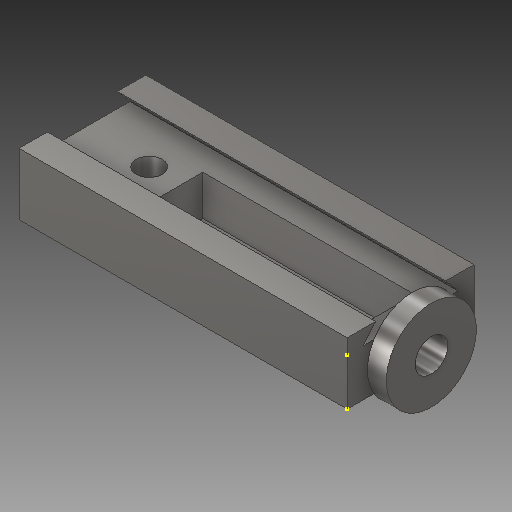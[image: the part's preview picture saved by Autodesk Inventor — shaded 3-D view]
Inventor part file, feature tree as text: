
AUTODESK INVENTOR PART (.ipt)
format: ipt  version: 2018 (Build 220112000, 112)  size: 252,928 bytes
history: native  units: mm
features: sketch x12, extrude x10
ambient origin geometry x8: Origin, YZ Plane, XZ Plane, XY Plane, X Axis, Y Axis, Z Axis, Center Point
bodies: Solid1 (feature_tree)
feature tree (22):
  extrude  "Extrusion1"  Depth=41.4mm
  extrude  "Extrusion2"  Depth=220.0mm
  extrude  "Extrusion3"  Depth=301.25mm TaperAngle=0.0deg
  sketch  "Sketch4"  dims[d12=15.1mm d13=15.1mm]
  extrude  "Extrusion4"  Depth=15.1mm
  sketch  "Sketch6"  dims[d17=28.6mm d18=30.2mm]
  extrude  "Extrusion5"  Depth=26.9mm TaperAngle=0.0deg
  extrude  "Extrusion6"  Depth=30.2mm
  extrude  "Extrusion7"  Depth=11.0mm
  extrude  "Extrusion8"  Depth=60.4mm
  extrude  "Extrusion9"  Depth=12.7mm
  extrude  "Extrusion10"  TaperAngle=90.0deg  [1 undecoded]
  sketch  "Sketch1"  dims[d0=85.0mm d1=41.4mm]
  sketch  "Sketch2"  dims[d2=220.0mm d3=0.0mm d4=19.0mm]
  sketch  "Sketch3"  dims[d8=19.0mm d9=301.25mm d10=0.0mm]
  sketch  "Sketch5"  dims[d14=141.9mm d15=26.9mm d16=0.0mm]
  sketch  "Sketch7"  dims[d19=4.6mm d21=11.0mm]
  sketch  "Sketch8"  dims[d22=91.9mm d23=0.0mm d24=60.4mm]
  sketch  "Sketch9"  dims[d25=12.7mm d26=0.0mm d27=10.6mm]
  sketch  "Sketch10"  dims[d28=83.6mm d29=90.0deg]
  sketch  "Sketch11"  dims[d30=4.9mm]
  sketch  "Sketch12"  dims[d31=6.0mm d32=0.0mm d33=22.0mm d34=22.3mm d35=22.7mm d36=22.15mm d37=0.0mm d38=4.6mm d39=0.0mm d40=17.5mm d41=310.85mm d42=0.0mm d43=4.4mm d44=5.0mm d45=4.4mm d46=2.5mm d47=3.5mm d48=0.0mm d49=40.7mm d50=9.4mm d51=4.0mm d52=40.7mm d53=9.4mm d54=4.0mm d55=70.6mm d56=39.5mm d57=4.5mm d58=4.5mm d59=7.0mm d60=0.0mm d61=8.726646mm d63=8.726646mm d64=10.0mm]
note: 1 required parameter value undecoded (feature->parameter linkage not recoverable at this tier; creation-order binding heuristic only, values carry confidence <= 0.55)
